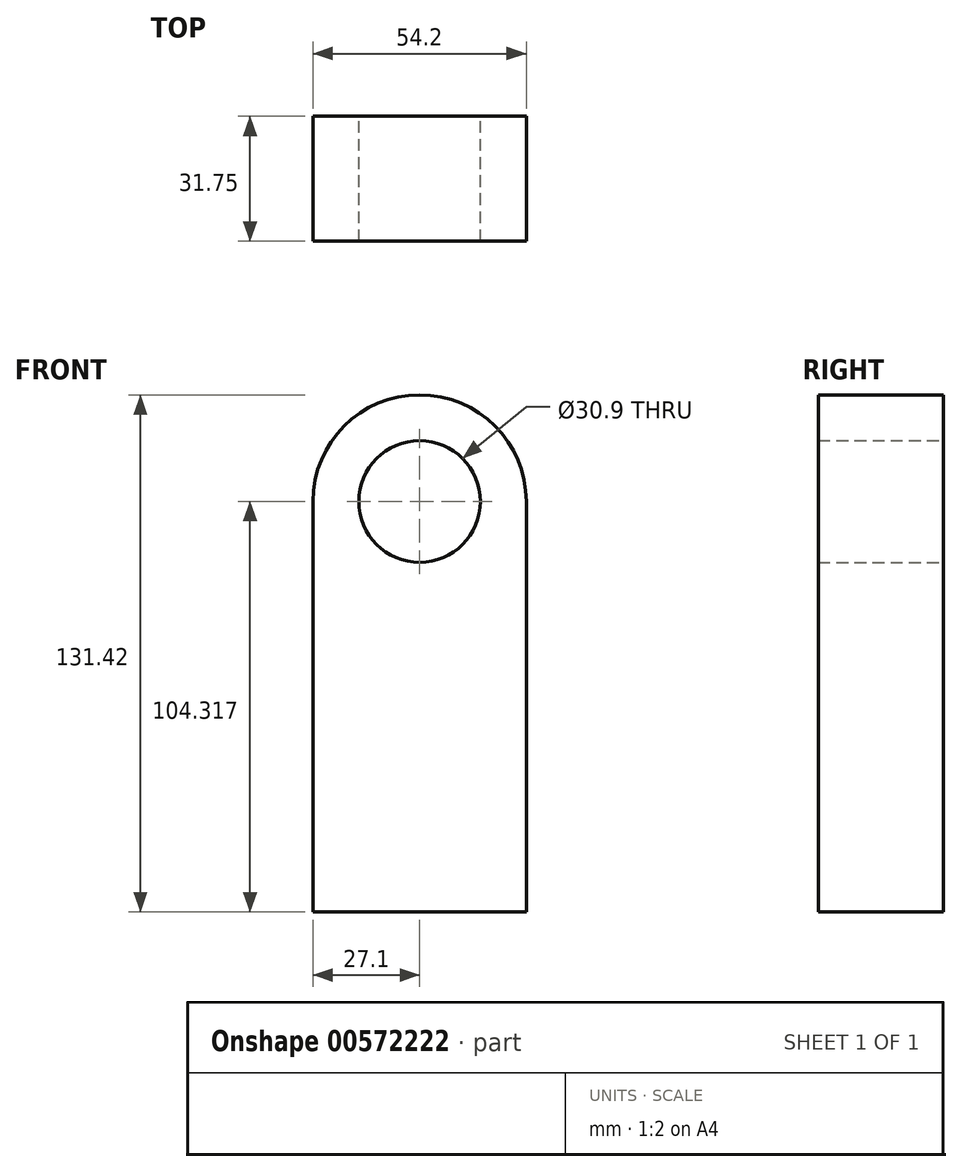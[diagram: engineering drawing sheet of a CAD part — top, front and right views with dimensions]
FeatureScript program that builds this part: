
annotation { "Feature Type Name" : "Feature", "Feature Type Description" : "" }
export const myFeature = defineFeature(function(context is Context, id is Id, definition is map)
    precondition{}
    {
        {
            var Q0;
            Q0=qCreatedBy(makeId("Front.planeOp"),FACE);
            var sketch = newSketch(context, id + "F0", { "sketchPlane" : qUnion([Q0])});
            skLineSegment(sketch, "E0.top", {"start": v(27.1, -52.16) * mm, "end": v(-27.1, -52.16) * mm});
            skLineSegment(sketch, "E0.left", {"start": v(27.1, 52.16) * mm, "end": v(27.1, -52.16) * mm});
            skLineSegment(sketch, "E0.right", {"start": v(-27.1, 52.16) * mm, "end": v(-27.1, -52.16) * mm});
            skPoint(sketch, "E0.middle", {"position": v(0, 0) * mm});
            skArc(sketch, "E1", {"start": v(27.1, 52.16) * mm, "mid": v(0, 79.26) * mm, "end": v(-27.1, 52.16) * mm});
            skCircle(sketch, "E2", {"center": v(0, 52.16) * mm, "radius": 15.45 * mm});
            skSolve(sketch);
        }
        {
            var Q0;
            Q0=makeQuery(id+"F0.imprint","IMPRINT",FACE,{"disambiguationData":[TD([[makeQuery(id+"F0.imprint","IMPRINT",EDGE,{"derivedFrom":sQuery(id+"F0.wireOp",EDGE,"E0.top")}),-1.0]])]});
            extrude(context, id + "F1", {"entities" : qUnion([Q0]), "depth" : 31.75 * mm, "offsetDistance" : 25.4 * mm});
        }
    });
